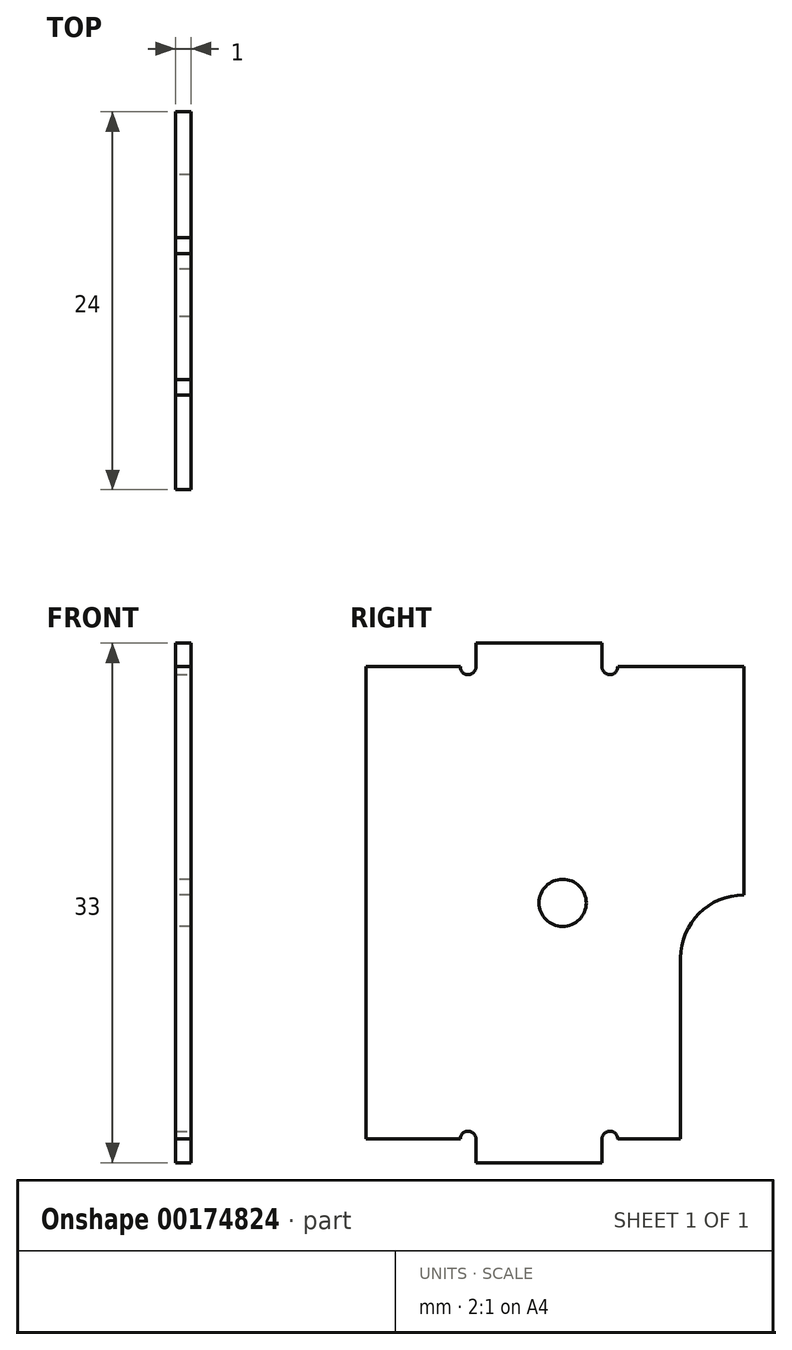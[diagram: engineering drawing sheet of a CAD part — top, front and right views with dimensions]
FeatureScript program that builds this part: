
annotation { "Feature Type Name" : "Feature", "Feature Type Description" : "" }
export const myFeature = defineFeature(function(context is Context, id is Id, definition is map)
    precondition{}
    {
        {
            var Q0;
            Q0=qCreatedBy(makeId("Right.planeOp"),FACE);
            var sketch = newSketch(context, id + "F0", { "sketchPlane" : qUnion([Q0])});
            skLineSegment(sketch, "E0.bottom", {"start": v(0, 0) * mm, "end": v(7, 0) * mm});
            skLineSegment(sketch, "E0.top", {"start": v(0, 30) * mm, "end": v(7, 30) * mm});
            skLineSegment(sketch, "E0.left", {"start": v(0, 0) * mm, "end": v(0, 30) * mm});
            skLineSegment(sketch, "E0.right", {"start": v(24, 15.5) * mm, "end": v(24, 30) * mm});
            skCircle(sketch, "E1", {"center": v(12.5, 15) * mm, "radius": 1.5 * mm});
            skPoint(sketch, "E1.centerSnap0", {"position": v(0, 15) * mm});
            skLineSegment(sketch, "E2", {"start": v(20, 0) * mm, "end": v(20, 15.5) * mm});
            skLineSegment(sketch, "E3", {"start": v(20, 15.5) * mm, "end": v(24, 15.5) * mm});
            skLineSegment(sketch, "E4.top", {"start": v(7, -1.5) * mm, "end": v(15, -1.5) * mm});
            skLineSegment(sketch, "E4.left", {"start": v(7, 0) * mm, "end": v(7, -1.5) * mm});
            skLineSegment(sketch, "E4.right", {"start": v(15, 0) * mm, "end": v(15, -1.5) * mm});
            skLineSegment(sketch, "E5.trimOffspring", {"start": v(15, 0) * mm, "end": v(20, 0) * mm});
            skLineSegment(sketch, "E6.top", {"start": v(7, 31.5) * mm, "end": v(15, 31.5) * mm});
            skLineSegment(sketch, "E6.left", {"start": v(7, 30) * mm, "end": v(7, 31.5) * mm});
            skLineSegment(sketch, "E6.right", {"start": v(15, 30) * mm, "end": v(15, 31.5) * mm});
            skLineSegment(sketch, "E7.trimOffspring", {"start": v(15, 30) * mm, "end": v(24, 30) * mm});
            skSolve(sketch);
        }
        {
            var Q0;
            Q0 = qSketchRegion(id + "F0", true);
            extrude(context, id + "F1", {"entities" : qUnion([Q0]), "depth" : 1 * mm});
        }
        {
            var Q0;
            Q0=makeQuery(id+"F1.opExtrude","SWEPT_EDGE",EDGE,{"disambiguationData":[OSD([sQuery(id+"F0.wireOp",EDGE,"E2"),sQuery(id+"F0.wireOp",EDGE,"E3")])]});
            fillet(context, id + "F2", {"entities" : qUnion([Q0]), "radius" : 4 * mm, "tangentPropagation" : true, "allowEdgeOverflow" : false});
        }
        {
            var Q0;
            Q0=makeQuery(id+"F1.opExtrude","CAP_FACE",FACE,{"disambiguationData":[OSD([sQuery(id+"F0.wireOp",EDGE,"E0.bottom"),sQuery(id+"F0.wireOp",EDGE,"E0.top"),sQuery(id+"F0.wireOp",EDGE,"E0.left"),sQuery(id+"F0.wireOp",EDGE,"E0.right"),sQuery(id+"F0.wireOp",EDGE,"E1"),sQuery(id+"F0.wireOp",EDGE,"E2"),sQuery(id+"F0.wireOp",EDGE,"E3"),sQuery(id+"F0.wireOp",EDGE,"E4.top"),sQuery(id+"F0.wireOp",EDGE,"E4.left"),sQuery(id+"F0.wireOp",EDGE,"E4.right"),sQuery(id+"F0.wireOp",EDGE,"E5.trimOffspring"),sQuery(id+"F0.wireOp",EDGE,"E6.top"),sQuery(id+"F0.wireOp",EDGE,"E6.left"),sQuery(id+"F0.wireOp",EDGE,"E6.right"),sQuery(id+"F0.wireOp",EDGE,"E7.trimOffspring")])],"isStart":false});
            var sketch = newSketch(context, id + "F3", { "sketchPlane" : qUnion([Q0])});
            skCircle(sketch, "E8", {"center": v(6.5, 30) * mm, "radius": 0.5 * mm});
            skCircle(sketch, "E9", {"center": v(15.5, 30) * mm, "radius": 0.5 * mm});
            skCircle(sketch, "E10", {"center": v(6.5, 0) * mm, "radius": 0.5 * mm});
            skCircle(sketch, "E11", {"center": v(15.5, 0) * mm, "radius": 0.5 * mm});
            skSolve(sketch);
        }
        {
            var Q0;
            Q0 = qSketchRegion(id + "F3", true);
            extrude(context, id + "F4", {"entities" : qUnion([Q0]), "operationType" : NewBodyOperationType.REMOVE, "oppositeDirection" : true, "depth" : 25 * mm});
        }
    });
